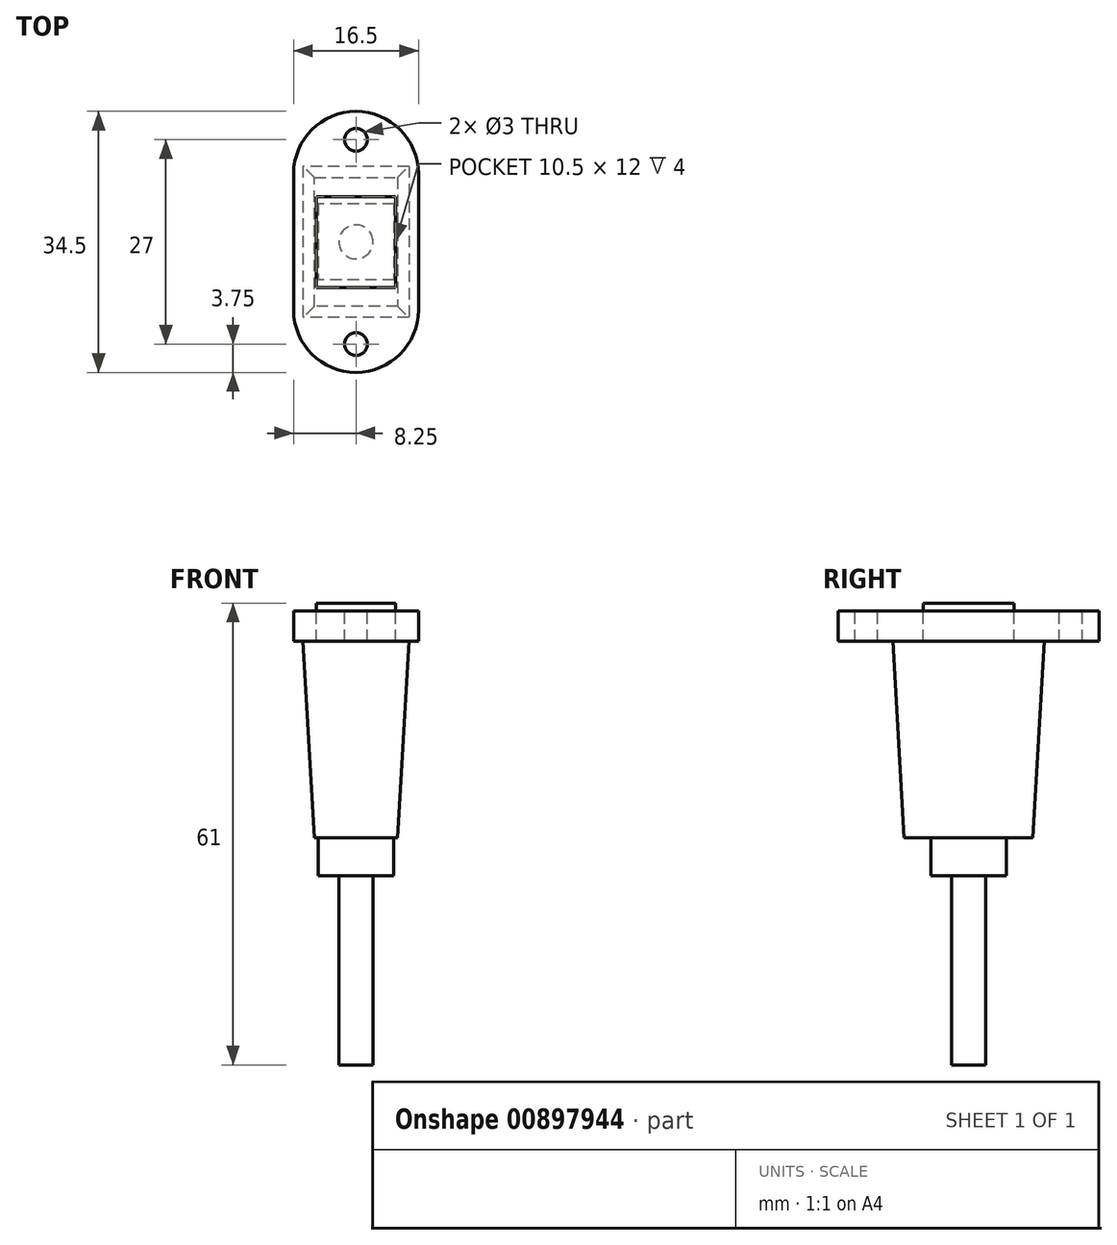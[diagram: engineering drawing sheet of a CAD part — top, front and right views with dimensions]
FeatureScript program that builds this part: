
annotation { "Feature Type Name" : "Feature", "Feature Type Description" : "" }
export const myFeature = defineFeature(function(context is Context, id is Id, definition is map)
    precondition{}
    {
        {
            var Q0;
            Q0=qCreatedBy(makeId("Top.planeOp"),FACE);
            var sketch = newSketch(context, id + "F0", { "sketchPlane" : qUnion([Q0])});
            skLineSegment(sketch, "E0.bottom", {"start": v(5.25, -6) * mm, "end": v(-5.25, -6) * mm});
            skLineSegment(sketch, "E0.top", {"start": v(5.25, 6) * mm, "end": v(-5.25, 6) * mm});
            skLineSegment(sketch, "E0.left", {"start": v(5.25, -6) * mm, "end": v(5.25, 6) * mm});
            skLineSegment(sketch, "E0.right", {"start": v(-5.25, -6) * mm, "end": v(-5.25, 6) * mm});
            skPoint(sketch, "E0.middle", {"position": v(0, 0) * mm});
            skLineSegment(sketch, "E1.bottom", {"start": v(8.25, -9) * mm, "end": v(-8.25, -9) * mm});
            skLineSegment(sketch, "E1.top", {"start": v(8.25, 9) * mm, "end": v(-8.25, 9) * mm});
            skLineSegment(sketch, "E1.left", {"start": v(8.25, -9) * mm, "end": v(8.25, 9) * mm});
            skLineSegment(sketch, "E1.right", {"start": v(-8.25, -9) * mm, "end": v(-8.25, 9) * mm});
            skArc(sketch, "E2", {"start": v(8.25, 9) * mm, "mid": v(0, 17.25) * mm, "end": v(-8.25, 9) * mm});
            skArc(sketch, "E3", {"start": v(8.25, -9) * mm, "mid": v(0, -17.25) * mm, "end": v(-8.25, -9) * mm});
            skCircle(sketch, "E4", {"center": v(0, 13.5) * mm, "radius": 1.5 * mm});
            skCircle(sketch, "E5", {"center": v(0, -13.5) * mm, "radius": 1.5 * mm});
            skSolve(sketch);
        }
        {
            var Q0;
            Q0=makeQuery(id+"F0.imprint","IMPRINT",FACE,{"disambiguationData":[TD([[makeQuery(id+"F0.imprint","IMPRINT",EDGE,{"derivedFrom":sQuery(id+"F0.wireOp",EDGE,"E0.bottom")}),1.0]])]});
            var Q1;
            Q1=makeQuery(id+"F0.imprint","IMPRINT",FACE,{"disambiguationData":[TD([[makeQuery(id+"F0.imprint","IMPRINT",EDGE,{"derivedFrom":sQuery(id+"F0.wireOp",EDGE,"E1.top")}),-1.0]])]});
            var Q2;
            Q2=makeQuery(id+"F0.imprint","IMPRINT",FACE,{"disambiguationData":[TD([[makeQuery(id+"F0.imprint","IMPRINT",EDGE,{"derivedFrom":sQuery(id+"F0.wireOp",EDGE,"E1.bottom")}),1.0]])]});
            extrude(context, id + "F1", {"entities" : qUnion([Q0, Q1, Q2]), "oppositeDirection" : true, "depth" : 4 * mm, "offsetDistance" : 25 * mm});
        }
        {
            var Q0;
            Q0=makeQuery(id+"F1.opExtrude","CAP_FACE",FACE,{"disambiguationData":[OSD([sQuery(id+"F0.wireOp",EDGE,"E0.bottom"),sQuery(id+"F0.wireOp",EDGE,"E0.top"),sQuery(id+"F0.wireOp",EDGE,"E0.left"),sQuery(id+"F0.wireOp",EDGE,"E0.right"),sQuery(id+"F0.wireOp",EDGE,"E1.left"),sQuery(id+"F0.wireOp",EDGE,"E1.right"),sQuery(id+"F0.wireOp",EDGE,"E2"),sQuery(id+"F0.wireOp",EDGE,"E3"),sQuery(id+"F0.wireOp",EDGE,"E4"),sQuery(id+"F0.wireOp",EDGE,"E5")])],"isStart":false});
            var sketch = newSketch(context, id + "F2", { "sketchPlane" : qUnion([Q0])});
            skLineSegment(sketch, "E6.bottom", {"start": v(7, -10) * mm, "end": v(-7, -10) * mm});
            skLineSegment(sketch, "E6.top", {"start": v(7, 10) * mm, "end": v(-7, 10) * mm});
            skLineSegment(sketch, "E6.left", {"start": v(7, -10) * mm, "end": v(7, 10) * mm});
            skLineSegment(sketch, "E6.right", {"start": v(-7, -10) * mm, "end": v(-7, 10) * mm});
            skPoint(sketch, "E6.middle", {"position": v(0, 0) * mm});
            skSolve(sketch);
        }
        {
            var Q0;
            Q0 = qSketchRegion(id + "F2", true);
            extrude(context, id + "F3", {"entities" : qUnion([Q0]), "operationType" : NewBodyOperationType.ADD, "depth" : 26 * mm, "offsetDistance" : 25 * mm});
        }
        {
            var Q0;
            Q0=makeQuery(id+"F3.opExtrude","CAP_EDGE",EDGE,{"disambiguationData":[OSD([sQuery(id+"F2.wireOp",EDGE,"E6.top")])],"isStart":false});
            var Q1;
            Q1=makeQuery(id+"F3.opExtrude","CAP_EDGE",EDGE,{"disambiguationData":[OSD([sQuery(id+"F2.wireOp",EDGE,"E6.bottom")])],"isStart":false});
            var Q2;
            Q2=makeQuery(id+"F3.opExtrude","CAP_EDGE",EDGE,{"disambiguationData":[OSD([sQuery(id+"F2.wireOp",EDGE,"E6.left")])],"isStart":false});
            var Q3;
            Q3=makeQuery(id+"F3.opExtrude","CAP_EDGE",EDGE,{"disambiguationData":[OSD([sQuery(id+"F2.wireOp",EDGE,"E6.right")])],"isStart":false});
            chamfer(context, id + "F4", {"entities" : qUnion([Q0, Q1, Q2, Q3]), "chamferType" : ChamferType.TWO_OFFSETS, "width1" : 1.5 * mm, "oppositeDirection" : false, "width2" : 26 * mm, "tangentPropagation" : true});
        }
        {
            var Q0;
            Q0=makeQuery(id+"F3.opExtrude","CAP_FACE",FACE,{"disambiguationData":[OSD([sQuery(id+"F2.wireOp",EDGE,"E6.bottom"),sQuery(id+"F2.wireOp",EDGE,"E6.top"),sQuery(id+"F2.wireOp",EDGE,"E6.left"),sQuery(id+"F2.wireOp",EDGE,"E6.right")])],"isStart":false});
            var sketch = newSketch(context, id + "F5", { "sketchPlane" : qUnion([Q0])});
            skLineSegment(sketch, "E7.bottom", {"start": v(5, -5) * mm, "end": v(-5, -5) * mm});
            skLineSegment(sketch, "E7.top", {"start": v(5, 5) * mm, "end": v(-5, 5) * mm});
            skLineSegment(sketch, "E7.left", {"start": v(5, -5) * mm, "end": v(5, 5) * mm});
            skLineSegment(sketch, "E7.right", {"start": v(-5, -5) * mm, "end": v(-5, 5) * mm});
            skPoint(sketch, "E7.middle", {"position": v(0, 0) * mm});
            skSolve(sketch);
        }
        {
            var Q0;
            Q0 = qSketchRegion(id + "F5", true);
            extrude(context, id + "F6", {"entities" : qUnion([Q0]), "operationType" : NewBodyOperationType.ADD, "depth" : 5 * mm, "offsetDistance" : 25 * mm});
        }
        {
            var Q0;
            Q0=makeQuery(id+"F6.opExtrude","CAP_FACE",FACE,{"disambiguationData":[OSD([sQuery(id+"F5.wireOp",EDGE,"E7.bottom"),sQuery(id+"F5.wireOp",EDGE,"E7.top"),sQuery(id+"F5.wireOp",EDGE,"E7.left"),sQuery(id+"F5.wireOp",EDGE,"E7.right")])],"isStart":false});
            var sketch = newSketch(context, id + "F7", { "sketchPlane" : qUnion([Q0])});
            skCircle(sketch, "E8", {"center": v(0, 0) * mm, "radius": 2.25 * mm});
            skSolve(sketch);
        }
        {
            var Q0;
            Q0 = qSketchRegion(id + "F7", true);
            extrude(context, id + "F8", {"entities" : qUnion([Q0]), "operationType" : NewBodyOperationType.ADD, "depth" : 25 * mm, "offsetDistance" : 25 * mm});
        }
        {
            var Q0;
            Q0=makeQuery(id+"F0.imprint","IMPRINT",FACE,{"disambiguationData":[TD([[makeQuery(id+"F0.imprint","IMPRINT",EDGE,{"derivedFrom":sQuery(id+"F0.wireOp",EDGE,"E0.bottom")}),1.0]])]});
            var sketch = newSketch(context, id + "F9", { "sketchPlane" : qUnion([Q0])});
            skLineSegment(sketch, "E9.bottom", {"start": v(5.25, 6) * mm, "end": v(-5.25, 6) * mm});
            skLineSegment(sketch, "E9.top", {"start": v(5.25, -6) * mm, "end": v(-5.25, -6) * mm});
            skLineSegment(sketch, "E9.left", {"start": v(5.25, 6) * mm, "end": v(5.25, -6) * mm});
            skLineSegment(sketch, "E9.right", {"start": v(-5.25, 6) * mm, "end": v(-5.25, -6) * mm});
            skPoint(sketch, "E9.middle", {"position": v(0, 0) * mm});
            skSolve(sketch);
        }
        {
            var Q0;
            Q0 = qSketchRegion(id + "F9", true);
            extrude(context, id + "F10", {"entities" : qUnion([Q0]), "operationType" : NewBodyOperationType.ADD, "depth" : 1 * mm, "offsetDistance" : 25 * mm});
        }
    });
